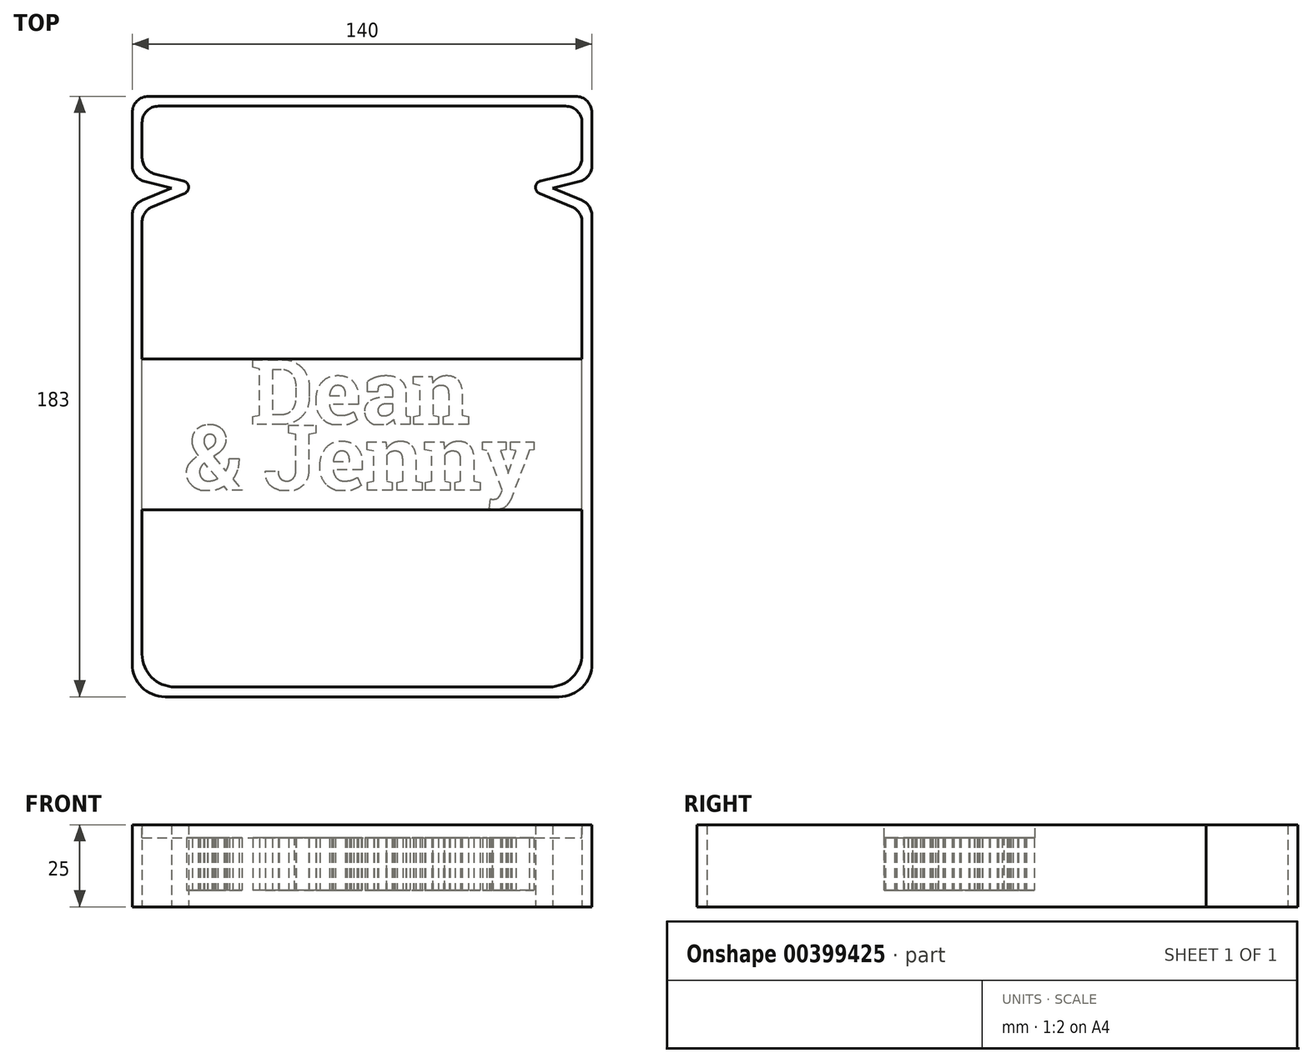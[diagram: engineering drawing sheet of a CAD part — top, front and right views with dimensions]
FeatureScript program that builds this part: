
annotation { "Feature Type Name" : "Feature", "Feature Type Description" : "" }
export const myFeature = defineFeature(function(context is Context, id is Id, definition is map)
    precondition{}
    {
        {
            var Q0;
            Q0=qCreatedBy(makeId("Top.planeOp"),FACE);
            var sketch = newSketch(context, id + "F0", { "sketchPlane" : qUnion([Q0])});
            skText(sketch, "E0", { "text": "Dean", "fontName": "RobotoSlab-Bold.ttf"});
            skText(sketch, "E1", { "text": "& Jenny", "fontName": "RobotoSlab-Bold.ttf"});
            skLineSegment(sketch, "E2.bottom", {"start": v(-54.06, -20) * mm, "end": v(54.06, -20) * mm});
            skLineSegment(sketch, "E2.top", {"start": v(-54.06, 0) * mm, "end": v(54.06, 0) * mm});
            skLineSegment(sketch, "E2.left", {"start": v(-54.06, -20) * mm, "end": v(-54.06, 0) * mm});
            skLineSegment(sketch, "E2.right", {"start": v(54.06, -20) * mm, "end": v(54.06, 0) * mm});
            skLineSegment(sketch, "E3.bottom", {"start": v(-34.06, 20) * mm, "end": v(34.06, 20) * mm});
            skLineSegment(sketch, "E3.top", {"start": v(-34.06, 0) * mm, "end": v(34.06, 0) * mm});
            skLineSegment(sketch, "E3.left", {"start": v(-34.06, 20) * mm, "end": v(-34.06, 0) * mm});
            skLineSegment(sketch, "E3.right", {"start": v(34.06, 20) * mm, "end": v(34.06, 0) * mm});
            skLineSegment(sketch, "E4.bottom", {"start": v(17, 0) * mm, "end": v(12.5, 0) * mm});
            skLineSegment(sketch, "E5.bottom", {"start": v(8, 0) * mm, "end": v(1, 0) * mm});
            const initialGuessF0  = {"E0": [-0.03406, 0, 1, 0, 0.02], "E1": [-0.05406, -0.02, 1, 0, 0.02]};
            skSetInitialGuess(sketch, initialGuessF0);
            skSolve(sketch);
        }
        {
            var Q0;
            {var subQ1=sQuery(id+"F0.wireOp",EDGE,"E1.sketch_text.stroke-181");Q0=makeQuery(id+"F0.imprint","IMPRINT",FACE,{"disambiguationData":[TD([[makeQuery(id+"F0.imprint","IMPRINT",EDGE,{"derivedFrom":subQ1}),-1.0]])]});}
            var Q1;
            Q1=makeQuery(id+"F0.imprint","IMPRINT",FACE,{"disambiguationData":[TD([[makeQuery(id+"F0.imprint","IMPRINT",EDGE,{"derivedFrom":sQuery(id+"F0.wireOp",EDGE,"E1.sketch_text.stroke-151")}),-1.0]])]});
            var Q2;
            Q2=makeQuery(id+"F0.imprint","IMPRINT",FACE,{"disambiguationData":[TD([[makeQuery(id+"F0.imprint","IMPRINT",EDGE,{"derivedFrom":sQuery(id+"F0.wireOp",EDGE,"E1.sketch_text.stroke-121")}),-1.0]])]});
            var Q3;
            Q3=makeQuery(id+"F0.imprint","IMPRINT",FACE,{"disambiguationData":[TD([[makeQuery(id+"F0.imprint","IMPRINT",EDGE,{"derivedFrom":sQuery(id+"F0.wireOp",EDGE,"E1.sketch_text.stroke-107")}),-1.0]])]});
            var Q4;
            {var subQ8=sQuery(id+"F0.wireOp",EDGE,"E1.sketch_text.stroke-100");Q4=makeQuery(id+"F0.imprint","IMPRINT",FACE,{"disambiguationData":[TD([[makeQuery(id+"F0.imprint","IMPRINT",EDGE,{"derivedFrom":subQ8}),-1.0]])]});}
            var Q5;
            {var subQ4=sQuery(id+"F0.wireOp",EDGE,"E1.sketch_text.stroke-74");Q5=makeQuery(id+"F0.imprint","IMPRINT",FACE,{"disambiguationData":[TD([[makeQuery(id+"F0.imprint","IMPRINT",EDGE,{"derivedFrom":subQ4}),-1.0]])]});}
            var Q6;
            Q6=makeQuery(id+"F0.imprint","IMPRINT",FACE,{"disambiguationData":[TD([[makeQuery(id+"F0.imprint","IMPRINT",EDGE,{"derivedFrom":sQuery(id+"F0.wireOp",EDGE,"E1.sketch_text.stroke-42")}),-1.0]])]});
            var Q7;
            Q7=makeQuery(id+"F0.imprint","IMPRINT",FACE,{"disambiguationData":[TD([[makeQuery(id+"F0.imprint","IMPRINT",EDGE,{"derivedFrom":sQuery(id+"F0.wireOp",EDGE,"E1.sketch_text.stroke-0")}),-1.0]])]});
            var Q8;
            Q8=makeQuery(id+"F0.imprint","IMPRINT",FACE,{"disambiguationData":[TD([[makeQuery(id+"F0.imprint","IMPRINT",EDGE,{"derivedFrom":sQuery(id+"F0.wireOp",EDGE,"E0.sketch_text.stroke-0")}),-1.0]])]});
            var Q9;
            {var subQ4=sQuery(id+"F0.wireOp",EDGE,"E0.sketch_text.stroke-31");Q9=makeQuery(id+"F0.imprint","IMPRINT",FACE,{"disambiguationData":[TD([[makeQuery(id+"F0.imprint","IMPRINT",EDGE,{"derivedFrom":subQ4}),-1.0]])]});}
            var Q10;
            {var subQ1=sQuery(id+"F0.wireOp",EDGE,"E0.sketch_text.stroke-66");Q10=makeQuery(id+"F0.imprint","IMPRINT",FACE,{"disambiguationData":[TD([[makeQuery(id+"F0.imprint","IMPRINT",EDGE,{"derivedFrom":subQ1}),-1.0]])]});}
            var Q11;
            {var subQ5=sQuery(id+"F0.wireOp",EDGE,"E0.sketch_text.stroke-88");Q11=makeQuery(id+"F0.imprint","IMPRINT",FACE,{"disambiguationData":[TD([[makeQuery(id+"F0.imprint","IMPRINT",EDGE,{"derivedFrom":subQ5}),-1.0]])]});}
            var Q12;
            {var subQ1=sQuery(id+"F0.wireOp",EDGE,"E1.sketch_text.stroke-117");Q12=makeQuery(id+"F0.imprint","IMPRINT",FACE,{"disambiguationData":[TD([[makeQuery(id+"F0.imprint","IMPRINT",EDGE,{"derivedFrom":subQ1}),-1.0]])]});}
            var Q13;
            {var subQ0=sQuery(id+"F0.wireOp",EDGE,"E1.sketch_text.stroke-138");Q13=makeQuery(id+"F0.imprint","IMPRINT",FACE,{"disambiguationData":[TD([[makeQuery(id+"F0.imprint","IMPRINT",EDGE,{"derivedFrom":subQ0}),-1.0]])]});}
            extrude(context, id + "F1", {"entities" : qUnion([Q0, Q1, Q2, Q3, Q4, Q5, Q6, Q7, Q8, Q9, Q10, Q11, Q12, Q13]), "depth" : 24 * mm, "hasSecondDirection" : true, "secondDirectionOppositeDirection" : false, "secondDirectionDepth" : 5 * mm});
        }
        {
            var Q0;
            Q0=qCreatedBy(makeId("Top.planeOp"),FACE);
            var sketch = newSketch(context, id + "F2", { "sketchPlane" : qUnion([Q0])});
            skLineSegment(sketch, "E6.bottom", {"start": v(-70, -83) * mm, "end": v(70, -83) * mm});
            skLineSegment(sketch, "E6.top", {"start": v(-70, 100) * mm, "end": v(70, 100) * mm});
            skLineSegment(sketch, "E6.right", {"start": v(70, -83) * mm, "end": v(70, 67) * mm});
            skLineSegment(sketch, "E7", {"start": v(-70, 75) * mm, "end": v(-58, 72) * mm});
            skLineSegment(sketch, "E8", {"start": v(-58, 72) * mm, "end": v(-70, 67) * mm});
            skLineSegment(sketch, "E9.MirrorCS", {"start": v(58, 72) * mm, "end": v(70, 67) * mm});
            skLineSegment(sketch, "E10.MirrorCS", {"start": v(70, 75) * mm, "end": v(58, 72) * mm});
            skLineSegment(sketch, "E11.trimOffspring", {"start": v(-70, 75) * mm, "end": v(-70, 100) * mm});
            skLineSegment(sketch, "E12.trimOffspring", {"start": v(70, 75) * mm, "end": v(70, 100) * mm});
            skLineSegment(sketch, "E13", {"start": v(-70, 67) * mm, "end": v(-70, -83) * mm});
            skLineSegment(sketch, "E14.bottom", {"start": v(-67, -80) * mm, "end": v(0, -80) * mm});
            skLineSegment(sketch, "E14.left", {"start": v(-67, -80) * mm, "end": v(-67, 65) * mm});
            skLineSegment(sketch, "E15.bottom", {"start": v(-67, 97) * mm, "end": v(0, 97) * mm});
            skLineSegment(sketch, "E15.left", {"start": v(-67, 97) * mm, "end": v(-67, 77.34) * mm});
            skLineSegment(sketch, "E16", {"start": v(-48.49, 72.71) * mm, "end": v(-67, 77.34) * mm});
            skLineSegment(sketch, "E17", {"start": v(0, 97) * mm, "end": v(0, -80) * mm, "construction": true});
            skLineSegment(sketch, "E18", {"start": v(-67, 65) * mm, "end": v(-48.49, 72.71) * mm});
            skLineSegment(sketch, "E19.MirrorCS", {"start": v(67, 97) * mm, "end": v(0, 97) * mm});
            skLineSegment(sketch, "E20.MirrorCS", {"start": v(67, 97) * mm, "end": v(67, 77.34) * mm});
            skLineSegment(sketch, "E21.MirrorCS", {"start": v(48.49, 72.71) * mm, "end": v(67, 77.34) * mm});
            skLineSegment(sketch, "E22.MirrorCS", {"start": v(67, 65) * mm, "end": v(48.49, 72.71) * mm});
            skLineSegment(sketch, "E23.MirrorCS", {"start": v(67, -80) * mm, "end": v(67, 65) * mm});
            skLineSegment(sketch, "E24.MirrorCS", {"start": v(67, -80) * mm, "end": v(0, -80) * mm});
            skSolve(sketch);
        }
        {
            var Q0;
            Q0=makeQuery(id+"F2.imprint","IMPRINT",FACE,{"disambiguationData":[TD([[makeQuery(id+"F2.imprint","IMPRINT",EDGE,{"derivedFrom":sQuery(id+"F2.wireOp",EDGE,"E6.bottom")}),1.0]])]});
            extrude(context, id + "F3", {"entities" : qUnion([Q0]), "operationType" : NewBodyOperationType.ADD, "depth" : 25 * mm});
        }
        {
            var Q0;
            Q0=makeQuery(id+"F3.opExtrude","CAP_FACE",FACE,{"disambiguationData":[OSD([sQuery(id+"F2.wireOp",EDGE,"E6.bottom"),sQuery(id+"F2.wireOp",EDGE,"E6.top"),sQuery(id+"F2.wireOp",EDGE,"E6.right"),sQuery(id+"F2.wireOp",EDGE,"E7"),sQuery(id+"F2.wireOp",EDGE,"E8"),sQuery(id+"F2.wireOp",EDGE,"E9.MirrorCS"),sQuery(id+"F2.wireOp",EDGE,"E10.MirrorCS"),sQuery(id+"F2.wireOp",EDGE,"E11.trimOffspring"),sQuery(id+"F2.wireOp",EDGE,"E12.trimOffspring"),sQuery(id+"F2.wireOp",EDGE,"E13"),sQuery(id+"F2.wireOp",EDGE,"E14.bottom"),sQuery(id+"F2.wireOp",EDGE,"E14.left"),sQuery(id+"F2.wireOp",EDGE,"E15.bottom"),sQuery(id+"F2.wireOp",EDGE,"E15.left"),sQuery(id+"F2.wireOp",EDGE,"E16"),sQuery(id+"F2.wireOp",EDGE,"E18"),sQuery(id+"F2.wireOp",EDGE,"E19.MirrorCS"),sQuery(id+"F2.wireOp",EDGE,"E20.MirrorCS"),sQuery(id+"F2.wireOp",EDGE,"E21.MirrorCS"),sQuery(id+"F2.wireOp",EDGE,"E22.MirrorCS"),sQuery(id+"F2.wireOp",EDGE,"E23.MirrorCS"),sQuery(id+"F2.wireOp",EDGE,"E24.MirrorCS")])],"isStart":false});
            var sketch = newSketch(context, id + "F4", { "sketchPlane" : qUnion([Q0])});
            skLineSegment(sketch, "E25.bottom", {"start": v(-70, 20) * mm, "end": v(70, 20) * mm});
            skLineSegment(sketch, "E25.top", {"start": v(-70, -26) * mm, "end": v(70, -26) * mm});
            skLineSegment(sketch, "E25.left", {"start": v(-70, 20) * mm, "end": v(-70, -26) * mm});
            skLineSegment(sketch, "E25.right", {"start": v(70, 20) * mm, "end": v(70, -26) * mm});
            skSolve(sketch);
        }
        {
            var Q0;
            {var subQ0=sQuery(id+"F4.wireOp",EDGE,"E25.bottom");var subQ1=makeQuery(id+"F3.opExtrude","CAP_EDGE",EDGE,{"disambiguationData":[OSD([sQuery(id+"F2.wireOp",EDGE,"E14.left")])],"isStart":false});var subQ2=makeQuery(id+"F4.imprint","INTERSECT",VERTEX,{"derivedFrom":[subQ1,subQ0]});Q0=makeQuery(id+"F4.imprint","IMPRINT",FACE,{"disambiguationData":[TD([[makeQuery(id+"F4.imprint","IMPRINT",EDGE,{"disambiguationData":[TD([[subQ2,-1.0]])],"derivedFrom":subQ0}),-1.0]])]});}
            extrude(context, id + "F5", {"entities" : qUnion([Q0]), "operationType" : NewBodyOperationType.ADD, "oppositeDirection" : true, "depth" : 4 * mm});
        }
        {
            var Q0;
            Q0=makeQuery(id+"F3.opExtrude","SWEPT_EDGE",EDGE,{"disambiguationData":[OSD([sQuery(id+"F2.wireOp",EDGE,"E14.bottom"),sQuery(id+"F2.wireOp",EDGE,"E14.left")])]});
            var Q1;
            Q1=makeQuery(id+"F3.opExtrude","SWEPT_EDGE",EDGE,{"disambiguationData":[OSD([sQuery(id+"F2.wireOp",EDGE,"E23.MirrorCS"),sQuery(id+"F2.wireOp",EDGE,"E24.MirrorCS")])]});
            var Q2;
            Q2=makeQuery(id+"F3.opExtrude","SWEPT_EDGE",EDGE,{"disambiguationData":[OSD([sQuery(id+"F2.wireOp",EDGE,"E6.bottom"),sQuery(id+"F2.wireOp",EDGE,"E6.right")])]});
            var Q3;
            Q3=makeQuery(id+"F3.opExtrude","SWEPT_EDGE",EDGE,{"disambiguationData":[OSD([sQuery(id+"F2.wireOp",EDGE,"E6.bottom"),sQuery(id+"F2.wireOp",EDGE,"E13")])]});
            fillet(context, id + "F6", {"entities" : qUnion([Q0, Q1, Q2, Q3]), "radius" : 10 * mm, "tangentPropagation" : true, "allowEdgeOverflow" : false});
        }
        {
            var Q0;
            Q0=makeQuery(id+"F3.opExtrude","SWEPT_EDGE",EDGE,{"disambiguationData":[OSD([sQuery(id+"F2.wireOp",EDGE,"E6.top"),sQuery(id+"F2.wireOp",EDGE,"E11.trimOffspring")])]});
            var Q1;
            Q1=makeQuery(id+"F3.opExtrude","SWEPT_EDGE",EDGE,{"disambiguationData":[OSD([sQuery(id+"F2.wireOp",EDGE,"E15.bottom"),sQuery(id+"F2.wireOp",EDGE,"E15.left")])]});
            var Q2;
            Q2=makeQuery(id+"F3.opExtrude","SWEPT_EDGE",EDGE,{"disambiguationData":[OSD([sQuery(id+"F2.wireOp",EDGE,"E6.top"),sQuery(id+"F2.wireOp",EDGE,"E12.trimOffspring")])]});
            var Q3;
            Q3=makeQuery(id+"F3.opExtrude","SWEPT_EDGE",EDGE,{"disambiguationData":[OSD([sQuery(id+"F2.wireOp",EDGE,"E19.MirrorCS"),sQuery(id+"F2.wireOp",EDGE,"E20.MirrorCS")])]});
            var Q4;
            Q4=makeQuery(id+"F3.opExtrude","SWEPT_EDGE",EDGE,{"disambiguationData":[OSD([sQuery(id+"F2.wireOp",EDGE,"E20.MirrorCS"),sQuery(id+"F2.wireOp",EDGE,"E21.MirrorCS")])]});
            var Q5;
            Q5=makeQuery(id+"F3.opExtrude","SWEPT_EDGE",EDGE,{"disambiguationData":[OSD([sQuery(id+"F2.wireOp",EDGE,"E10.MirrorCS"),sQuery(id+"F2.wireOp",EDGE,"E12.trimOffspring")])]});
            var Q6;
            Q6=makeQuery(id+"F3.opExtrude","SWEPT_EDGE",EDGE,{"disambiguationData":[OSD([sQuery(id+"F2.wireOp",EDGE,"E15.left"),sQuery(id+"F2.wireOp",EDGE,"E16")])]});
            var Q7;
            Q7=makeQuery(id+"F3.opExtrude","SWEPT_EDGE",EDGE,{"disambiguationData":[OSD([sQuery(id+"F2.wireOp",EDGE,"E7"),sQuery(id+"F2.wireOp",EDGE,"E11.trimOffspring")])]});
            var Q8;
            Q8=makeQuery(id+"F3.opExtrude","SWEPT_EDGE",EDGE,{"disambiguationData":[OSD([sQuery(id+"F2.wireOp",EDGE,"E6.right"),sQuery(id+"F2.wireOp",EDGE,"E9.MirrorCS")])]});
            var Q9;
            Q9=makeQuery(id+"F3.opExtrude","SWEPT_EDGE",EDGE,{"disambiguationData":[OSD([sQuery(id+"F2.wireOp",EDGE,"E22.MirrorCS"),sQuery(id+"F2.wireOp",EDGE,"E23.MirrorCS")])]});
            var Q10;
            Q10=makeQuery(id+"F3.opExtrude","SWEPT_EDGE",EDGE,{"disambiguationData":[OSD([sQuery(id+"F2.wireOp",EDGE,"E8"),sQuery(id+"F2.wireOp",EDGE,"E13")])]});
            var Q11;
            Q11=makeQuery(id+"F3.opExtrude","SWEPT_EDGE",EDGE,{"disambiguationData":[OSD([sQuery(id+"F2.wireOp",EDGE,"E14.left"),sQuery(id+"F2.wireOp",EDGE,"E18")])]});
            fillet(context, id + "F7", {"entities" : qUnion([Q0, Q1, Q2, Q3, Q4, Q5, Q6, Q7, Q8, Q9, Q10, Q11]), "radius" : 5 * mm, "tangentPropagation" : true, "allowEdgeOverflow" : false});
        }
        {
            var Q0;
            Q0=makeQuery(id+"F3.opExtrude","SWEPT_EDGE",EDGE,{"disambiguationData":[OSD([sQuery(id+"F2.wireOp",EDGE,"E21.MirrorCS"),sQuery(id+"F2.wireOp",EDGE,"E22.MirrorCS")])]});
            var Q1;
            Q1=makeQuery(id+"F3.opExtrude","SWEPT_EDGE",EDGE,{"disambiguationData":[OSD([sQuery(id+"F2.wireOp",EDGE,"E16"),sQuery(id+"F2.wireOp",EDGE,"E18")])]});
            fillet(context, id + "F8", {"entities" : qUnion([Q0, Q1]), "radius" : 2 * mm, "tangentPropagation" : true, "allowEdgeOverflow" : false});
        }
    });
